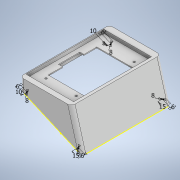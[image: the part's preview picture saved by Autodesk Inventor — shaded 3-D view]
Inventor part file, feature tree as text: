
AUTODESK INVENTOR PART (.ipt)
format: ipt  version: 2022 (Build 260153000, 153)  size: 411,648 bytes
history: native  units: mm
features: sketch x15, extrude x8, projected_geometry x6, sweep x3, plane x1
ambient origin geometry x8: Origin, YZ Plane, XZ Plane, XY Plane, X Axis, Y Axis, Z Axis, Center Point
bodies: Solid1 (feature_tree)
feature tree (33):
  extrude  "Extrusion1"  Depth=193.2mm
  extrude  "Extrusion2"  Depth=4.2mm
  extrude  "Extrusion3"  Depth=65.697mm
  extrude  "Extrusion4"  Depth=4.2mm
  extrude  "Extrusion5"  Depth=126.501mm
  extrude  "Extrusion6"  Depth=22.6mm
  extrude  "Extrusion7"  Depth=8.0mm
  sweep  "Sweep1"
  plane  "Work Plane1"
  extrude  "Extrusion8"  Depth=11.0mm
  sketch  "Sketch12"  dims[d19=6.0mm d20=7.5mm d21=0.0mm]
  sweep  "Sweep2"
  sweep  "Sweep3"
  sketch  "Sketch1"  dims[d0=110.94mm d1=193.2mm]
  sketch  "Sketch2"  dims[d2=4.2mm d3=4.2mm]
  projected_geometry  "Projected Loop1"
  sketch  "Sketch3"  dims[d4=65.3mm d5=65.697mm]
  sketch  "Sketch5"  dims[d6=4.2mm d7=4.2mm]
  projected_geometry  "Projected Loop2"
  sketch  "Sketch6"  dims[d8=126.2mm d9=126.501mm]
  sketch  "Sketch7"  dims[d10=0.0mm d11=22.6mm]
  projected_geometry  "Projected Loop3"
  sketch  "Sketch8"  dims[d12=35.0mm d13=8.0mm]
  sketch  "Sketch9"  dims[d14=2.0mm d15=0.0mm d16=2.0mm]
  sketch  "3D Sketch1"
  sketch  "Sketch11"  dims[d17=14.0mm d18=11.0mm]
  projected_geometry  "Projected Loop5"
  sketch  "Sketch13"  dims[d22=105.0mm d23=79.0mm]
  projected_geometry  "Projected Loop6"
  sketch  "3D Sketch2"
  sketch  "Sketch14"  dims[d24=6.0mm d25=30.0mm d26=40.0mm d27=40.0mm d28=9.0mm d29=7.5mm d30=0.0mm d39=2.0mm d40=72.0mm d41=0.0mm d42=23.5mm d47=4.083461mm d48=140.0mm d49=1000.0mm d50=0.0mm d51=23.1125mm d52=23.113mm d53=63.0mm d54=0.0mm d55=6.0mm d56=1000.0mm d57=0.0mm d58=8.0mm d59=0.0mm d60=0.0mm d62=90.0deg d64=2.0mm d65=1000.0mm d66=0.0mm d67=8.0mm d68=8.0mm d69=8.0mm d70=8.0mm d71=15.0mm d72=6.0mm d73=6.0mm d74=15.0mm d75=6.0mm d76=10.0mm d77=6.0mm d78=10.0mm d80=13.0mm d81=8.0mm d82=8.0mm d83=13.0mm d84=17.0mm d85=8.0mm d86=8.0mm d87=17.0mm d88=0.0mm d89=0.0mm d90=13.0mm d91=8.0mm d92=13.0mm d93=8.0mm d94=0.0mm d95=0.0mm]
  projected_geometry  "Projected Loop7"
  sketch  "3D Sketch3"
